# Revit family: Legalett_Prefabriserad_Plint
name_source: partatom
category: Structural Foundations
units: mm (PartAtom-declared; Revit-internal decimal feet)

## family parameters
Always vertical = Yes
Cap = No
Cut with Voids When Loaded = No
Material for Model Behavior = Other
Shared = No
Show family pre-cut in plan views = Yes
Work Plane-Based = No

## types (6) — shared parameters
Manufacturer = Legalett
Pad Type = P2
Volume = 0.5 m³

## per-type parameters (varying)
| type | Foundation Thickness | Pad Length | Type Comments | botten bredd | height | topp bredd |
| Betongplint 45 | 100 mm  [stored 0.328084 ft] | 500 mm  [stored 1.64042 ft] | 500x500x500 | 240 mm  [stored 0.787402 ft] | 500 mm  [stored 1.64042 ft] | 200 mm  [stored 0.656168 ft] |
| Betongplint 63 | 100 mm  [stored 0.328084 ft] | 500 mm  [stored 1.64042 ft] | 500x500x900 | 282 mm | 900 mm | 200 mm  [stored 0.656168 ft] |
| Betongplint 150 | 150 mm | 800 mm | 800x800x550 | 390 mm | 550 mm | 350 mm  [stored 1.14829 ft] |
| Betongplint 163 | 150 mm | 800 mm | 800x800x850 | 312 mm | 850 mm | 310 mm |
| Betongplint 220 | 150 mm | 800 mm | 800x800x950 | 432 mm  [stored 1.41732 ft] | 950 mm | 350 mm  [stored 1.14829 ft] |
| Betongplint 350 | 150 mm | 1000 mm  [stored 3.28084 ft] | 1000x1000x1750 | 352 mm | 1750 mm | 350 mm  [stored 1.14829 ft] |

note: column(s) folded — value = type name in every type: Model

note: [stored X ft] marks values corroborated as IEEE doubles in the binary element streams (Revit-internal decimal feet)

## geometry (parser evidence)
native form markers: Blend x4, Sweep x2
no freeform markers — native parametric forms only
